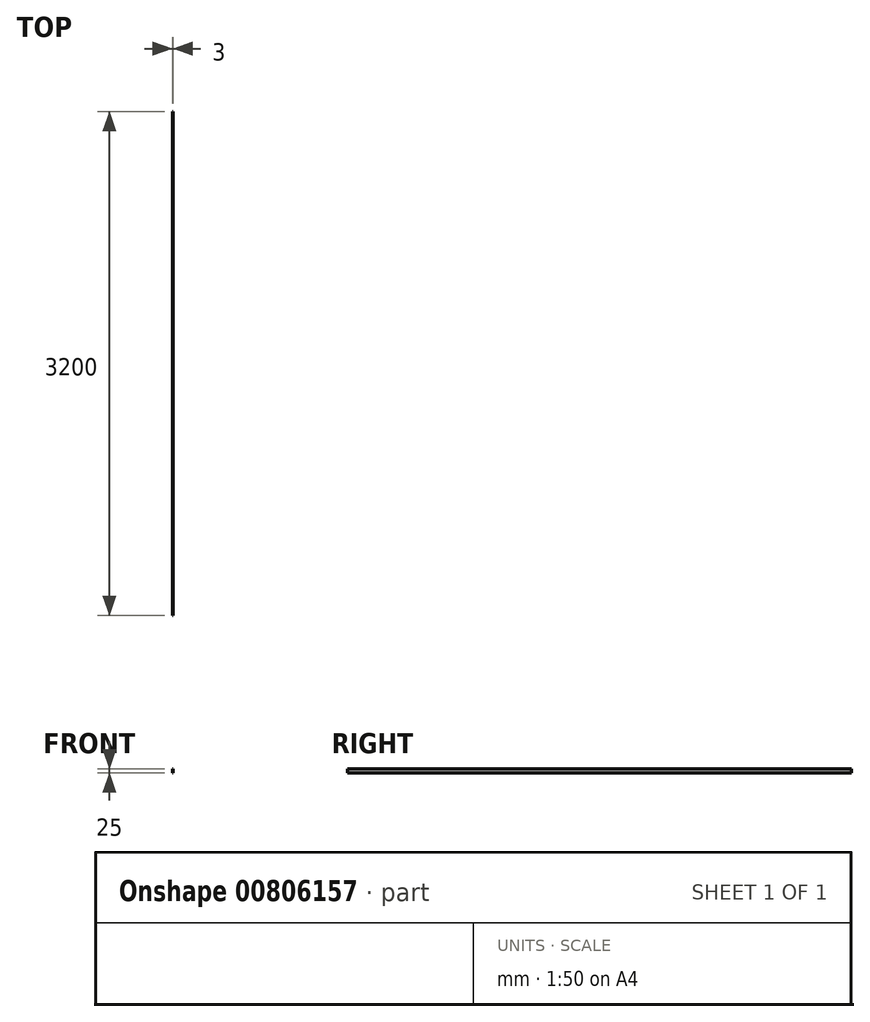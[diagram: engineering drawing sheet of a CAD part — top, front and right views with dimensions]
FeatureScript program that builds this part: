
annotation { "Feature Type Name" : "Feature", "Feature Type Description" : "" }
export const myFeature = defineFeature(function(context is Context, id is Id, definition is map)
    precondition{}
    {
        {
            var Q0;
            Q0=qCreatedBy(makeId("Front.planeOp"),FACE);
            var sketch = newSketch(context, id + "F0", { "sketchPlane" : qUnion([Q0])});
            skLineSegment(sketch, "E0.bottom", {"start": v(0, 16.59) * mm, "end": v(3, 16.59) * mm});
            skLineSegment(sketch, "E0.top", {"start": v(0, -8.41) * mm, "end": v(3, -8.41) * mm});
            skLineSegment(sketch, "E0.left", {"start": v(0, 16.59) * mm, "end": v(0, -8.41) * mm});
            skLineSegment(sketch, "E0.right", {"start": v(3, 16.59) * mm, "end": v(3, -8.41) * mm});
            skSolve(sketch);
        }
        {
            var Q0;
            Q0=qSketchRegion(id+"F0",true);
            extrude(context, id + "F1", {"entities" : qUnion([Q0]), "depth" : 3200 * mm, "offsetDistance" : 25 * mm});
        }
    });
